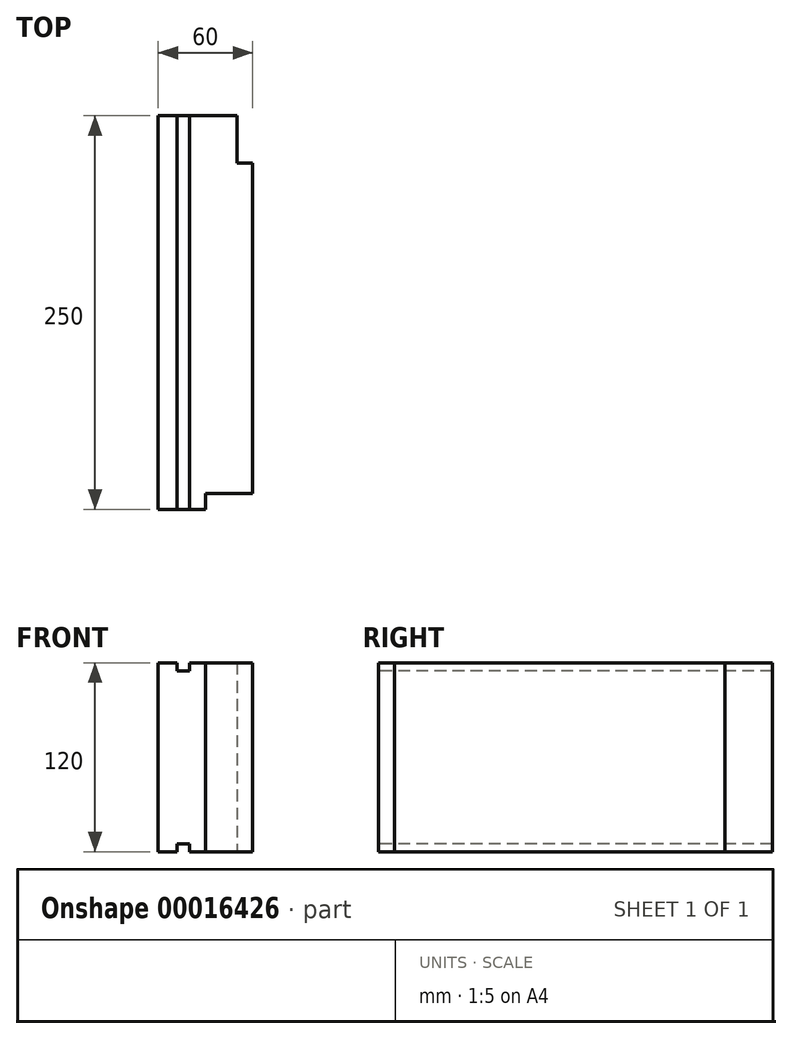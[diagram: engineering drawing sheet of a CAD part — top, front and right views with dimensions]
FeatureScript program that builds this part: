
annotation { "Feature Type Name" : "Feature", "Feature Type Description" : "" }
export const myFeature = defineFeature(function(context is Context, id is Id, definition is map)
    precondition{}
    {
        {
            var Q0;
            Q0=qCreatedBy(makeId("Top.planeOp"),FACE);
            var sketch = newSketch(context, id + "F0", { "sketchPlane" : qUnion([Q0])});
            skLineSegment(sketch, "E0.bottom", {"start": v(-175.01, -88.44) * mm, "end": v(-145.01, -88.44) * mm});
            skLineSegment(sketch, "E0.top", {"start": v(-175.01, 161.56) * mm, "end": v(-115.01, 161.56) * mm});
            skLineSegment(sketch, "E0.left", {"start": v(-175.01, -88.44) * mm, "end": v(-175.01, 161.56) * mm});
            skLineSegment(sketch, "E0.right", {"start": v(-115.01, -88.44) * mm, "end": v(-115.01, 131.56) * mm});
            skLineSegment(sketch, "E1.bottom", {"start": v(-115.01, 161.56) * mm, "end": v(114.99, 161.56) * mm});
            skLineSegment(sketch, "E1.top", {"start": v(-115.01, 101.56) * mm, "end": v(114.99, 101.56) * mm});
            skLineSegment(sketch, "E1.left", {"start": v(-115.01, 131.56) * mm, "end": v(-115.01, 101.56) * mm});
            skLineSegment(sketch, "E1.right", {"start": v(114.99, 131.56) * mm, "end": v(114.99, 101.56) * mm});
            skLineSegment(sketch, "E2.bottom", {"start": v(114.99, 161.56) * mm, "end": v(174.99, 161.56) * mm});
            skLineSegment(sketch, "E2.top", {"start": v(144.99, -88.44) * mm, "end": v(174.99, -88.44) * mm});
            skLineSegment(sketch, "E2.left", {"start": v(114.99, 131.56) * mm, "end": v(114.99, -88.44) * mm});
            skLineSegment(sketch, "E2.right", {"start": v(174.99, 161.56) * mm, "end": v(174.99, -88.44) * mm});
            skLineSegment(sketch, "E3.bottom", {"start": v(-115.01, 161.56) * mm, "end": v(-125.01, 161.56) * mm});
            skLineSegment(sketch, "E3.top", {"start": v(-115.01, 131.56) * mm, "end": v(-125.01, 131.56) * mm});
            skLineSegment(sketch, "E3.right", {"start": v(-125.01, 161.56) * mm, "end": v(-125.01, 131.56) * mm});
            skLineSegment(sketch, "E4.bottom", {"start": v(114.99, 161.56) * mm, "end": v(124.99, 161.56) * mm});
            skLineSegment(sketch, "E4.top", {"start": v(114.99, 131.56) * mm, "end": v(124.99, 131.56) * mm});
            skLineSegment(sketch, "E4.right", {"start": v(124.99, 161.56) * mm, "end": v(124.99, 131.56) * mm});
            skLineSegment(sketch, "E5.top", {"start": v(-175.01, -198.44) * mm, "end": v(-115.01, -198.44) * mm});
            skLineSegment(sketch, "E5.left", {"start": v(-175.01, -88.44) * mm, "end": v(-175.01, -198.44) * mm});
            skLineSegment(sketch, "E5.right", {"start": v(-115.01, -88.44) * mm, "end": v(-115.01, -198.44) * mm});
            skLineSegment(sketch, "E6.bottom", {"start": v(144.99, -88.44) * mm, "end": v(175.16, -88.44) * mm});
            skLineSegment(sketch, "E6.top", {"start": v(114.99, -198.44) * mm, "end": v(175.16, -198.44) * mm});
            skLineSegment(sketch, "E6.left", {"start": v(114.99, -88.44) * mm, "end": v(114.99, -198.44) * mm});
            skLineSegment(sketch, "E6.right", {"start": v(175.16, -88.44) * mm, "end": v(175.16, -198.44) * mm});
            skLineSegment(sketch, "E7.top", {"start": v(-115.01, -78.44) * mm, "end": v(-145.01, -78.44) * mm});
            skLineSegment(sketch, "E7.left", {"start": v(-115.01, -88.44) * mm, "end": v(-115.01, -78.44) * mm});
            skLineSegment(sketch, "E7.right", {"start": v(-145.01, -88.44) * mm, "end": v(-145.01, -78.44) * mm});
            skLineSegment(sketch, "E8.top", {"start": v(114.99, -78.44) * mm, "end": v(144.99, -78.44) * mm});
            skLineSegment(sketch, "E8.left", {"start": v(114.99, -88.44) * mm, "end": v(114.99, -78.44) * mm});
            skLineSegment(sketch, "E8.right", {"start": v(144.99, -88.44) * mm, "end": v(144.99, -78.44) * mm});
            skSolve(sketch);
        }
        {
            var Q0;
            Q0=makeQuery(id+"F0.imprint","IMPRINT",FACE,{"disambiguationData":[TD([[makeQuery(id+"F0.imprint","IMPRINT",EDGE,{"derivedFrom":sQuery(id+"F0.wireOp",EDGE,"E0.top")}),-1.0]])]});
            extrude(context, id + "F1", {"entities" : qUnion([Q0]), "depth" : 120 * mm});
        }
        {
            var Q0;
            Q0=makeQuery(id+"F1.opExtrude","CAP_FACE",FACE,{"disambiguationData":[OSD([sQuery(id+"F0.wireOp",EDGE,"E0.top"),sQuery(id+"F0.wireOp",EDGE,"E0.left"),sQuery(id+"F0.wireOp",EDGE,"E0.right"),sQuery(id+"F0.wireOp",EDGE,"E1.left"),sQuery(id+"F0.wireOp",EDGE,"E3.top"),sQuery(id+"F0.wireOp",EDGE,"E3.right"),sQuery(id+"F0.wireOp",EDGE,"E0.bottom"),sQuery(id+"F0.wireOp",EDGE,"E7.top"),sQuery(id+"F0.wireOp",EDGE,"E7.right")])],"isStart":false});
            var sketch = newSketch(context, id + "F2", { "sketchPlane" : qUnion([Q0])});
            skLineSegment(sketch, "E9.bottom", {"start": v(-163.01, 183.24) * mm, "end": v(-155.01, 183.24) * mm});
            skLineSegment(sketch, "E9.top", {"start": v(-163.01, -106.27) * mm, "end": v(-155.01, -106.27) * mm});
            skLineSegment(sketch, "E9.left", {"start": v(-163.01, 183.24) * mm, "end": v(-163.01, -106.27) * mm});
            skLineSegment(sketch, "E9.right", {"start": v(-155.01, 183.24) * mm, "end": v(-155.01, -106.27) * mm});
            skSolve(sketch);
        }
        {
            var Q0;
            {var subQ3=sQuery(id+"F2.wireOp",EDGE,"E9.left");var subQ5=makeQuery(id+"F1.opExtrude","CAP_EDGE",EDGE,{"disambiguationData":[OSD([sQuery(id+"F0.wireOp",EDGE,"E0.top")])],"isStart":false});var subQ7=makeQuery(id+"F2.imprint","INTERSECT",VERTEX,{"derivedFrom":[subQ5,subQ3]});Q0=makeQuery(id+"F2.imprint","IMPRINT",FACE,{"disambiguationData":[TD([[makeQuery(id+"F2.imprint","IMPRINT",EDGE,{"disambiguationData":[TD([[subQ7,-1.0]])],"derivedFrom":subQ3}),1.0]])]});}
            extrude(context, id + "F3", {"entities" : qUnion([Q0]), "operationType" : NewBodyOperationType.REMOVE, "oppositeDirection" : true, "depth" : 5 * mm});
        }
        {
            var Q0;
            Q0=makeQuery(id+"F1.opExtrude","CAP_FACE",FACE,{"disambiguationData":[OSD([sQuery(id+"F0.wireOp",EDGE,"E0.top"),sQuery(id+"F0.wireOp",EDGE,"E0.left"),sQuery(id+"F0.wireOp",EDGE,"E0.right"),sQuery(id+"F0.wireOp",EDGE,"E1.left"),sQuery(id+"F0.wireOp",EDGE,"E3.top"),sQuery(id+"F0.wireOp",EDGE,"E3.right"),sQuery(id+"F0.wireOp",EDGE,"E0.bottom"),sQuery(id+"F0.wireOp",EDGE,"E7.top"),sQuery(id+"F0.wireOp",EDGE,"E7.right")])],"isStart":true});
            var sketch = newSketch(context, id + "F4", { "sketchPlane" : qUnion([Q0])});
            skLineSegment(sketch, "E10.bottom", {"start": v(-163, -161.56) * mm, "end": v(-154.98, -161.56) * mm});
            skLineSegment(sketch, "E10.top", {"start": v(-163, 88.44) * mm, "end": v(-154.98, 88.44) * mm});
            skLineSegment(sketch, "E10.left", {"start": v(-163, -161.56) * mm, "end": v(-163, 88.44) * mm});
            skLineSegment(sketch, "E10.right", {"start": v(-154.98, -161.56) * mm, "end": v(-154.98, 88.44) * mm});
            skSolve(sketch);
        }
        {
            var Q0;
            Q0=makeQuery(id+"F4.imprint","IMPRINT",FACE,{"disambiguationData":[TD([[makeQuery(id+"F4.imprint","IMPRINT",EDGE,{"derivedFrom":sQuery(id+"F4.wireOp",EDGE,"E10.bottom")}),1.0]])]});
            extrude(context, id + "F5", {"entities" : qUnion([Q0]), "operationType" : NewBodyOperationType.REMOVE, "oppositeDirection" : true, "depth" : 5 * mm});
        }
    });
